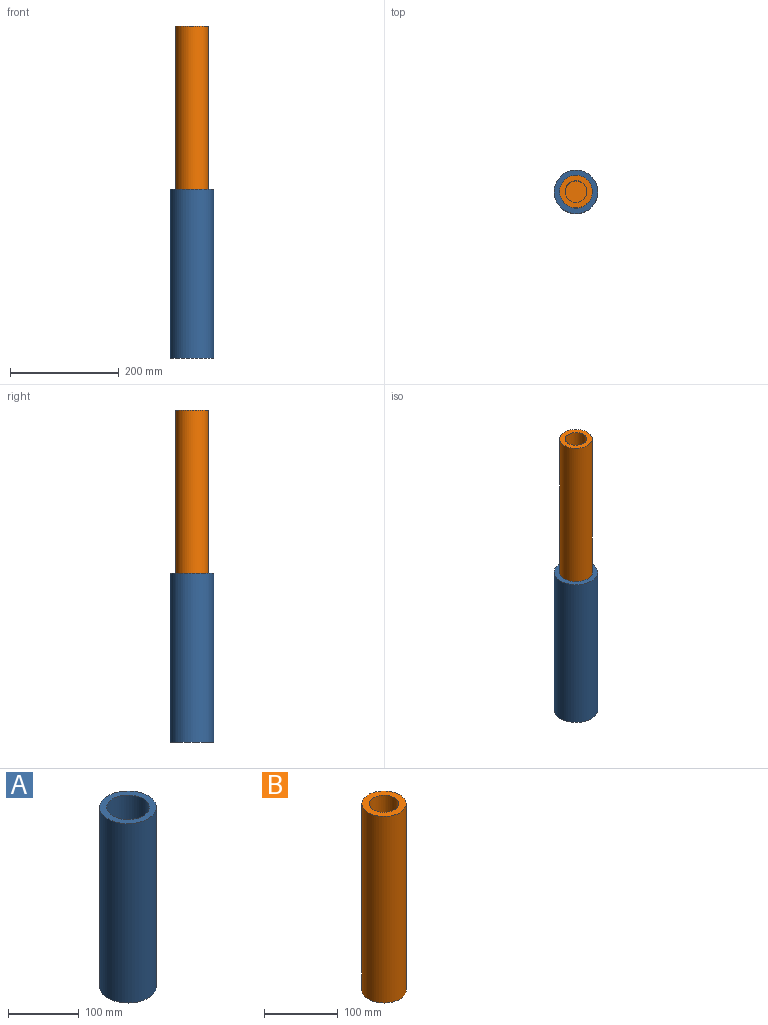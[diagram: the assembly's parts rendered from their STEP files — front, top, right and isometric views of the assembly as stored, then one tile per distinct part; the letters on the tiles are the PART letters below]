
ASSEMBLY  parts=2 mates=1
PART A: 5 faces, bbox 80x80x310 mm
  f0: cylinder r=30mm len=300mm, axis (0,0,1), area 56548.7mm2, adj f2,f3
  f1: cylinder r=40mm len=310mm, axis (0,0,1), area 77911.5mm2, adj f2,f4
  f2: plane 80x80mm, normal (0,0,1), area 2199.1mm2, adj f0,f1
  f3: plane 60x60mm, normal (0,0,1), area 2827.4mm2, adj f0
  f4: plane 80x80mm, normal (0,0,-1), area 5026.5mm2, adj f1
PART B: 5 faces, bbox 60x60x310 mm
  f0: cylinder r=20mm len=300mm, axis (0,0,1), area 37699.1mm2, adj f2,f3
  f1: cylinder r=30mm len=310mm, axis (0,0,1), area 58433.6mm2, adj f2,f4
  f2: plane 60x60mm, normal (0,0,1), area 1570.8mm2, adj f0,f1
  f3: plane 40x40mm, normal (0,0,1), area 1256.6mm2, adj f0
  f4: plane 60x60mm, normal (0,0,-1), area 2827.4mm2, adj f1
PLACE A at identity fixed
PLACE B t=(0,0,300)mm
MATE slider B.f0 <-> A.f0  axis (0,0,1) through (0,0,300)mm
